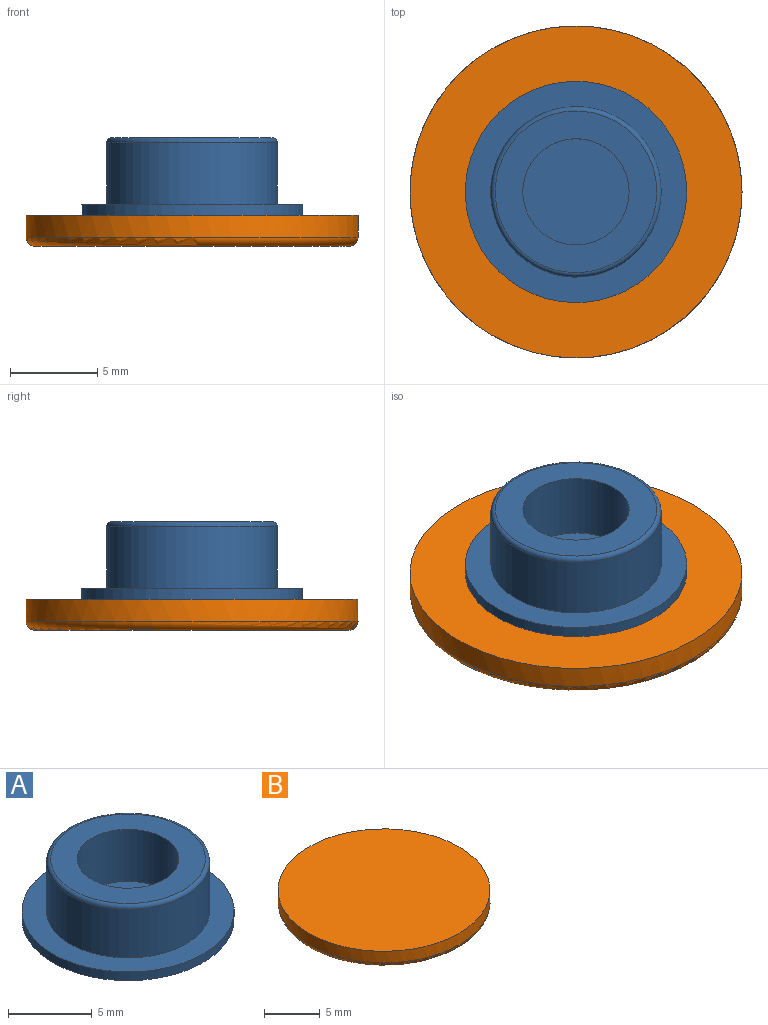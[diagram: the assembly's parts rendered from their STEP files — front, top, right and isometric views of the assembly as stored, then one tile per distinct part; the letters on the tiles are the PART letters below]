
ASSEMBLY  parts=2 mates=1
PART A: 8 faces, bbox 12.7x12.7x4.4 mm
  f0: cylinder r=3.05mm len=6.1mm, axis (0,0,-1), area 73mm2, adj f2,f6
  f1: cylinder r=4.89mm len=9.78mm, axis (0,0,-1), area 109.2mm2, adj f3,f7
  f2: plane 9.27x9.27mm, normal (0,0,1), area 38.3mm2, adj f0,f7
  f3: plane 12.7x12.7mm, normal (0,0,1), area 51.6mm2, adj f1,f5
  f4: plane 12.7x12.7mm, normal (0,0,-1), area 126.7mm2, adj f5
  f5: cylinder r=6.35mm len=12.7mm, axis (0,0,1), area 25.3mm2, adj f3,f4
  f6: plane 6.1x6.1mm, normal (0,0,1), area 29.2mm2, adj f0
  f7: torus R=4.64mm, axis (0,0,1), area 12mm2, adj f1,f2
PART B: 4 faces, bbox 20.6x20.6x1.8 mm
  f0: revolved ~17.8x17.8mm, area 252.4mm2, adj f3
  f1: cylinder r=9.53mm len=19.05mm, axis (0,0,1), area 75.2mm2, adj f2,f3
  f2: plane 19.05x19.05mm, normal (0,0,1), area 285mm2, adj f1
  f3: torus R=9.02mm, axis (0,0,-1), area 53.5mm2, adj f0,f1
PLACE A t=(-1.45,-1.1,1.85)mm
PLACE B t=(-1.45,-1.1,7.63)mm
MATE planar B.f1 <-> A.f0  axis (0,0,1) through (-1.45,-1.1,1.22)mm
